# Revit family: Bodenindikator KeDi 32
name_source: partatom
category: Allgemeines Modell
revit_build: Autodesk Revit 2016 (Build: 20161004_0715(x64)
units: mm (PartAtom-declared; Revit-internal decimal feet)

## family parameters
Arbeitsebenenbasiert = Nein
Beim Laden mit Abzugskörper schneiden = Nein
Bemaßung runder Anschluss = Durchmesser verwenden
Gemeinsam genutzt = Nein
Immer vertikal = Ja
Kann Basisbauteil für Bewehrung sein = Nein
Raumberechnungspunkt = Nein
Teiletyp = Normal

## types (4) — shared parameters
Auftrittsfläche = Rändelstruktur
Fasenausbildung = Minifase
Material = Hochleistungsfaserbeton
Norm = DIN 32984
Oberflächenausbildung = Kegelstumpf
Produktfamilie = Bodenindikator
Produktionsnorm = DIN V 18500
Produktname = KeDi32
Produzent = IKM Betonsteinwerk Knapp & Co GmbH, Muggensturm
RIL = 813.02.01
Rastermaß L/ B in mm = 300/300
www = www.Betonsteinwerk-Knapp.de

## per-type parameters (varying)
| type | 64.5 | 80.45 | Artikelnummer | Farbausführung | GTIN - Nummer | Gewicht/St | LRV-Wert | Materialität | R-Wert  nach DIN 51130 |
| KeDi 32  - 300/300/64,5 Weiß | Ja | Nein | 5-303208-470-00 | Nr. 470 Weiß | 4060851017066 | 12.2 | 53,06 | Nr. 470 Weiß | R12 |
| KeDi 32 - 300/300/64,5 Anthrazit | Ja | Nein | 5-303208-469-90 | Nr. 469 Anthrazit mit Oberflächenvergütung | 4060851017073 | 12.2 | 3,97 | Nr. 469 Anthrazit | R11 |
| KeDi 32  - 300/300/80,45 Weiß | Nein | Ja | 5-303208-470-00 | Nr. 470 Weiß | 4060851017066 | 16,6 | 53,06 | Nr. 470 Weiß | R12 |
| KeDi 32 - 300/300/80,45 Anthrazit | Nein | Ja | 5-303208-469-90 | Nr. 469 Anthrazit mit Oberflächenvergütung | 4060851017073 | 16,6 | 3,97 | Nr. 469 Anthrazit | R11 |
